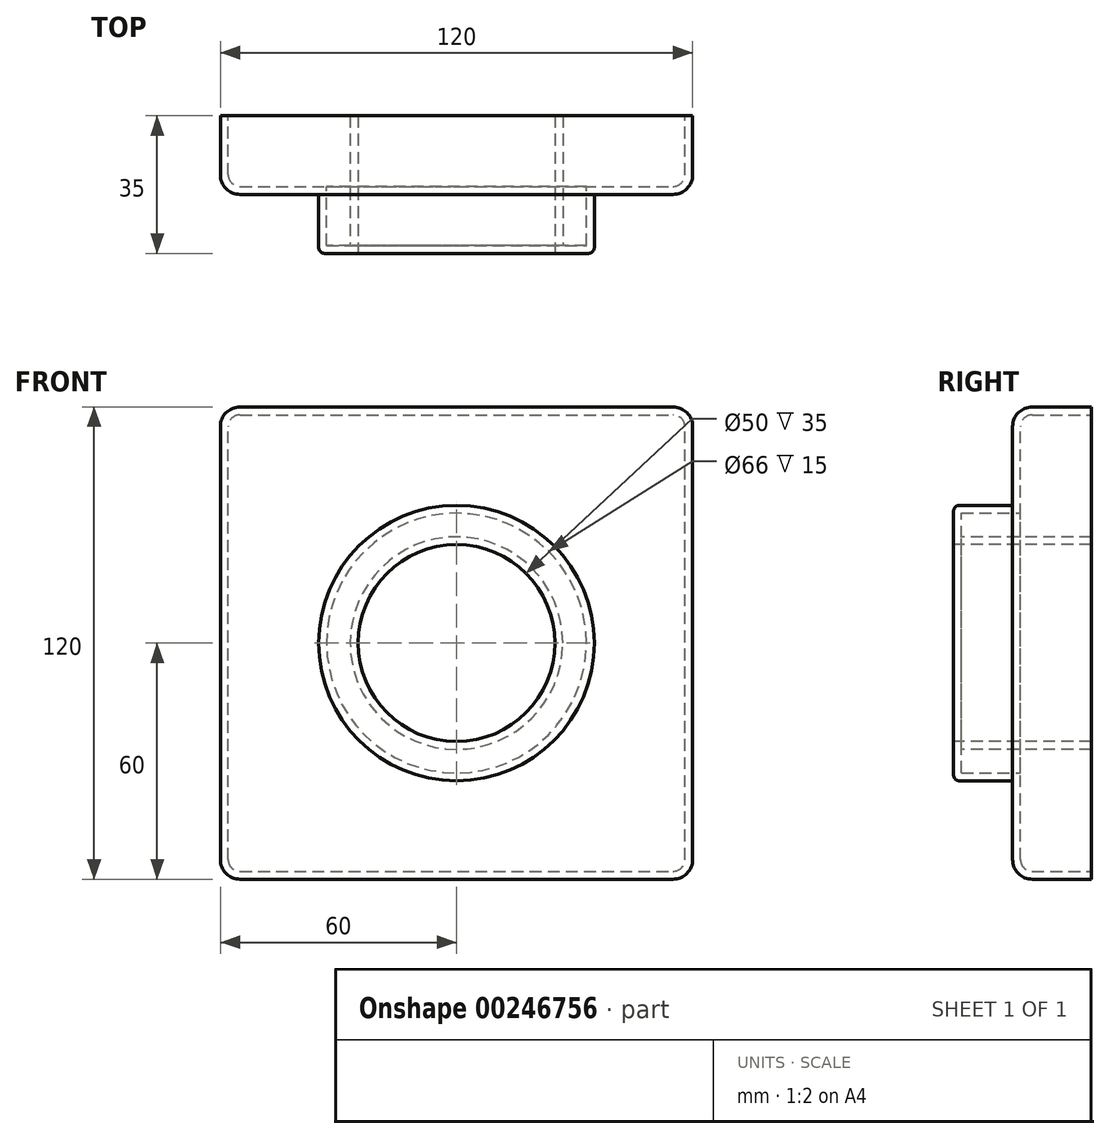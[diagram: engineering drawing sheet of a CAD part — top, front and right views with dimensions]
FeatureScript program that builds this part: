
annotation { "Feature Type Name" : "Feature", "Feature Type Description" : "" }
export const myFeature = defineFeature(function(context is Context, id is Id, definition is map)
    precondition{}
    {
        {
            var Q0;
            Q0=qCreatedBy(makeId("Front.planeOp"),FACE);
            var sketch = newSketch(context, id + "F4", { "sketchPlane" : qUnion([Q0])});
            skLineSegment(sketch, "E0.bottom", {"start": v(0, 0) * mm, "end": v(120, 0) * mm});
            skLineSegment(sketch, "E0.top", {"start": v(0, 120) * mm, "end": v(120, 120) * mm});
            skLineSegment(sketch, "E0.left", {"start": v(0, 0) * mm, "end": v(0, 120) * mm});
            skLineSegment(sketch, "E0.right", {"start": v(120, 0) * mm, "end": v(120, 120) * mm});
            skSolve(sketch);
        }
        {
            var Q0;
            Q0=makeQuery(id+"F4.imprint","IMPRINT",FACE,{"disambiguationData":[TD([[makeQuery(id+"F4.imprint","IMPRINT",EDGE,{"derivedFrom":sQuery(id+"F4.wireOp",EDGE,"E0.bottom")}),1.0]])]});
            extrude(context, id + "F0", {"entities" : qUnion([Q0]), "depth" : 20 * mm});
        }
        {
            var Q0;
            Q0=makeQuery(id+"F0.opExtrude","CAP_FACE",FACE,{"disambiguationData":[OSD([sQuery(id+"F4.wireOp",EDGE,"E0.bottom"),sQuery(id+"F4.wireOp",EDGE,"E0.top"),sQuery(id+"F4.wireOp",EDGE,"E0.left"),sQuery(id+"F4.wireOp",EDGE,"E0.right")])],"isStart":false});
            var sketch = newSketch(context, id + "F5", { "sketchPlane" : qUnion([Q0])});
            skLineSegment(sketch, "E1", {"start": v(0, 60) * mm, "end": v(120, 60) * mm, "construction": true});
            skLineSegment(sketch, "E2", {"start": v(60, 120) * mm, "end": v(60, 0) * mm, "construction": true});
            skCircle(sketch, "E3", {"center": v(60, 60) * mm, "radius": 35 * mm});
            skSolve(sketch);
        }
        {
            var Q0;
            Q0=makeQuery(id+"F5.imprint","IMPRINT",FACE,{"disambiguationData":[TD([[makeQuery(id+"F5.imprint","IMPRINT",EDGE,{"derivedFrom":sQuery(id+"F5.wireOp",EDGE,"E3")}),1.0]])]});
            extrude(context, id + "F1", {"entities" : qUnion([Q0]), "operationType" : NewBodyOperationType.ADD, "depth" : 15 * mm});
        }
        {
            var Q0;
            Q0=makeQuery(id+"F1.opExtrude","CAP_FACE",FACE,{"disambiguationData":[OSD([sQuery(id+"F5.wireOp",EDGE,"E3")])],"isStart":false});
            var sketch = newSketch(context, id + "F2", { "sketchPlane" : qUnion([Q0])});
            skCircle(sketch, "E4", {"center": v(60, 60) * mm, "radius": 25 * mm});
            skSolve(sketch);
        }
        {
            var Q0;
            Q0=makeQuery(id+"F2.imprint","IMPRINT",FACE,{"disambiguationData":[TD([[makeQuery(id+"F2.imprint","IMPRINT",EDGE,{"derivedFrom":sQuery(id+"F2.wireOp",EDGE,"E4")}),1.0]])]});
            var Q1;
            Q1=makeQuery(id+"F0.opExtrude","CAP_FACE",FACE,{"disambiguationData":[OSD([sQuery(id+"F4.wireOp",EDGE,"E0.bottom"),sQuery(id+"F4.wireOp",EDGE,"E0.top"),sQuery(id+"F4.wireOp",EDGE,"E0.left"),sQuery(id+"F4.wireOp",EDGE,"E0.right")])],"isStart":true});
            extrude(context, id + "F6", {"entities" : qUnion([Q0]), "operationType" : NewBodyOperationType.REMOVE, "endBound" : BoundingType.UP_TO_SURFACE, "oppositeDirection" : true, "endBoundEntityFace" : qUnion([Q1]), "depth" : 25 * mm});
        }
        {
            var Q0;
            Q0=makeQuery(id+"F0.opExtrude","SWEPT_EDGE",EDGE,{"disambiguationData":[OSD([sQuery(id+"F4.wireOp",EDGE,"E0.top"),sQuery(id+"F4.wireOp",EDGE,"E0.right")])]});
            var Q1;
            Q1=makeQuery(id+"F0.opExtrude","CAP_EDGE",EDGE,{"disambiguationData":[OSD([sQuery(id+"F4.wireOp",EDGE,"E0.top")])],"isStart":false});
            var Q2;
            Q2=makeQuery(id+"F0.opExtrude","CAP_EDGE",EDGE,{"disambiguationData":[OSD([sQuery(id+"F4.wireOp",EDGE,"E0.right")])],"isStart":false});
            var Q3;
            Q3=makeQuery(id+"F0.opExtrude","CAP_EDGE",EDGE,{"disambiguationData":[OSD([sQuery(id+"F4.wireOp",EDGE,"E0.bottom")])],"isStart":false});
            var Q4;
            Q4=makeQuery(id+"F0.opExtrude","CAP_EDGE",EDGE,{"disambiguationData":[OSD([sQuery(id+"F4.wireOp",EDGE,"E0.left")])],"isStart":false});
            var Q5;
            Q5=makeQuery(id+"F0.opExtrude","SWEPT_EDGE",EDGE,{"disambiguationData":[OSD([sQuery(id+"F4.wireOp",EDGE,"E0.top"),sQuery(id+"F4.wireOp",EDGE,"E0.left")])]});
            var Q6;
            Q6=makeQuery(id+"F0.opExtrude","SWEPT_EDGE",EDGE,{"disambiguationData":[OSD([sQuery(id+"F4.wireOp",EDGE,"E0.bottom"),sQuery(id+"F4.wireOp",EDGE,"E0.left")])]});
            var Q7;
            Q7=makeQuery(id+"F0.opExtrude","SWEPT_EDGE",EDGE,{"disambiguationData":[OSD([sQuery(id+"F4.wireOp",EDGE,"E0.bottom"),sQuery(id+"F4.wireOp",EDGE,"E0.right")])]});
            var Q8;
            Q8=makeQuery(id+"F1.opExtrude","CAP_EDGE",EDGE,{"disambiguationData":[OSD([sQuery(id+"F5.wireOp",EDGE,"E3")])],"isStart":true});
            fillet(context, id + "F3", {"entities" : qUnion([Q0, Q1, Q2, Q3, Q4, Q5, Q6, Q7, Q8]), "radius" : 5 * mm, "tangentPropagation" : true, "allowEdgeOverflow" : false});
        }
        {
            var Q0;
            Q0=makeQuery(id+"F1.opExtrude","CAP_EDGE",EDGE,{"disambiguationData":[OSD([sQuery(id+"F5.wireOp",EDGE,"E3")])],"isStart":false});
            var Q1;
            Q1=makeQuery(id+"F6.boolean.opBoolean","COPY",EDGE,{"derivedFrom":makeQuery(id+"F6.opExtrude","CAP_EDGE",EDGE,{"disambiguationData":[OSD([sQuery(id+"F2.wireOp",EDGE,"E4")])],"isStart":true})});
            fillet(context, id + "F7", {"entities" : qUnion([Q0, Q1]), "radius" : 1.5 * mm, "tangentPropagation" : true, "allowEdgeOverflow" : false});
        }
        {
            var Q0;
            Q0=makeQuery(id+"F0.opExtrude","CAP_FACE",FACE,{"disambiguationData":[OSD([sQuery(id+"F4.wireOp",EDGE,"E0.bottom"),sQuery(id+"F4.wireOp",EDGE,"E0.top"),sQuery(id+"F4.wireOp",EDGE,"E0.left"),sQuery(id+"F4.wireOp",EDGE,"E0.right")])],"isStart":true});
            shell(context, id + "F8", {"entities" : qUnion([Q0]), "thickness" : 2 * mm});
        }
    });
